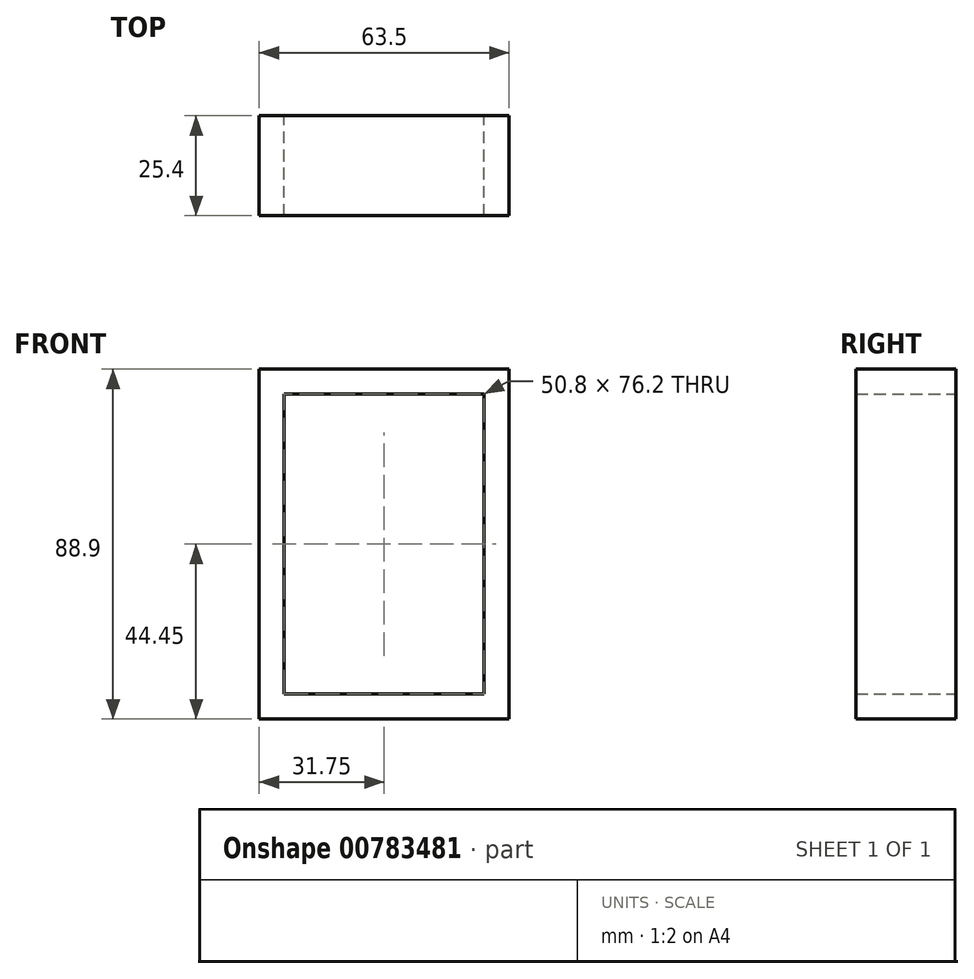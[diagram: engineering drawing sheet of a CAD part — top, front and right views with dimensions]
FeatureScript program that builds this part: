
annotation { "Feature Type Name" : "Feature", "Feature Type Description" : "" }
export const myFeature = defineFeature(function(context is Context, id is Id, definition is map)
    precondition{}
    {
        {
            var Q0;
            Q0=qCreatedBy(makeId("Front.planeOp"),FACE);
            var sketch = newSketch(context, id + "F0", { "sketchPlane" : qUnion([Q0])});
            skLineSegment(sketch, "E0.bottom", {"start": v(25.4, 38.1) * mm, "end": v(-25.4, 38.1) * mm});
            skLineSegment(sketch, "E0.top", {"start": v(25.4, -38.1) * mm, "end": v(-25.4, -38.1) * mm});
            skLineSegment(sketch, "E0.left", {"start": v(25.4, 38.1) * mm, "end": v(25.4, -38.1) * mm});
            skLineSegment(sketch, "E0.right", {"start": v(-25.4, 38.1) * mm, "end": v(-25.4, -38.1) * mm});
            skPoint(sketch, "E0.middle", {"position": v(0, 0) * mm});
            skLineSegment(sketch, "E1.0", {"start": v(31.75, 44.45) * mm, "end": v(-31.75, 44.45) * mm});
            skLineSegment(sketch, "E1.1", {"start": v(31.75, 44.45) * mm, "end": v(31.75, -44.45) * mm});
            skLineSegment(sketch, "E1.2", {"start": v(31.75, -44.45) * mm, "end": v(-31.75, -44.45) * mm});
            skLineSegment(sketch, "E1.3", {"start": v(-31.75, 44.45) * mm, "end": v(-31.75, -44.45) * mm});
            skSolve(sketch);
        }
        {
            var Q0;
            Q0=makeQuery(id+"F0.imprint","IMPRINT",FACE,{"disambiguationData":[TD([[makeQuery(id+"F0.imprint","IMPRINT",EDGE,{"derivedFrom":sQuery(id+"F0.wireOp",EDGE,"E0.bottom")}),-1.0]])]});
            extrude(context, id + "F1", {"entities" : qUnion([Q0]), "endBound" : BoundingType.SYMMETRIC, "depth" : 25.4 * mm, "offsetDistance" : 25.4 * mm});
        }
    });
